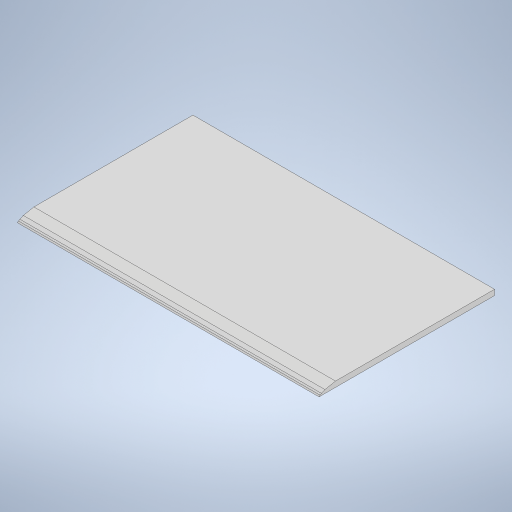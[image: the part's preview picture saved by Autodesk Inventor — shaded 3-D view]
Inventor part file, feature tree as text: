
AUTODESK INVENTOR PART (.ipt)
format: ipt  version: 2024 (Build 280153000, 153)  size: 228,352 bytes
history: native  units: mm
features: chamfer x4, extrude x2, sketch x2
ambient origin geometry x8: Origin, YZ Plane, XZ Plane, XY Plane, X Axis, Y Axis, Z Axis, Center Point
bodies: Solid1 (feature_tree)
feature tree (8):
  extrude  "Extrusion1"  Depth=110.0mm
  extrude  "Extrusion2"  Depth=2.0mm TaperAngle=0.0deg
  chamfer  "Chamfer4"  Distance=2.0mm Angle=45.0deg
  chamfer  "Chamfer5"  Distance=2.0mm Angle=45.0deg
  chamfer  "Chamfer6"  Distance=2.0mm Angle=45.0deg
  chamfer  "Chamfer7"  Distance=2.0mm Angle=45.0deg
  sketch  "Sketch1"  dims[d0=110.0mm d1=50.0mm]
  sketch  "Sketch2"  dims[d2=2.0mm d3=0.0mm d13=14.0mm d14=0.0mm d15=2.0mm d16=2.0mm d17=45.0deg d18=2.0mm d19=2.0mm d20=45.0deg d21=2.0mm d22=2.0mm d23=45.0deg d24=0.3mm d25=2.0mm d26=45.0deg]
